# Revit family: VOLCANO_VR_1_AC_01
name_source: partatom
category: Mechanical Equipment
revit_build: Autodesk Revit 2017 (Build: 20170118_1100(x64)
units: mm (PartAtom-declared; Revit-internal decimal feet)

## family parameters
Cut with Voids When Loaded = No
Host = Face
Part Type = Normal
Room Calculation Point = No
Round Connector Dimension = Use Diameter
Shared = No

## types (3) — shared parameters
Connection stub pipe diameter inlet = 19 "
Connection stub pipe diameter outlet = 19 "
Default Elevation = 1219 mm
Device inlet air temperature = 0 °C
Device inlet water temperature = 70 °C
Device outlet water temperature = 50 °C
Electrical Potential = 230 V
Frequency = 50 Hz
Manufacturer = VTS
Motor rated current AC = 1 A
Motor rated rotations [rpm] = 1380
Protection rating = IP 54
Show Range = Yes
URL = http://vtsgroup.pl
Weight = 27.50 kg

## per-type parameters (varying)
| type | AC motor power | Device heating power | Device outlet air temperature | Fan output | Heat exchanger pressure loss | Horizontal range | Medium flow | Model | Vertical range |
| VOLCANO VR 1 HIGH | 280 W | 22 kW | 12 °C | 5300 m³/h | 13.50 Pa | 23000 mm  [stored 75.4593 ft] | 2 m³/h | VR 1 HIGH | 12000 mm  [stored 39.3701 ft] |
| VOLCANO VR 1 MEDIUM | 220 W | 18 kW | 14 °C | 3900 m³/h | 10.80 Pa | 20000 mm  [stored 65.6168 ft] | 1 m³/h | VR 1 MEDIUM | 9000 mm |
| VOLCANO VR 1 LOW | 190 W | 15 kW | 16 °C | 2800 m³/h | 7.80 Pa | 15000 mm  [stored 49.2126 ft] | 1 m³/h | VR 1 LOW | 7000 mm  [stored 22.9659 ft] |

note: [stored X ft] marks values corroborated as IEEE doubles in the binary element streams (Revit-internal decimal feet)

## geometry (parser evidence)
native form markers: Sweep x9
no freeform markers — native parametric forms only
